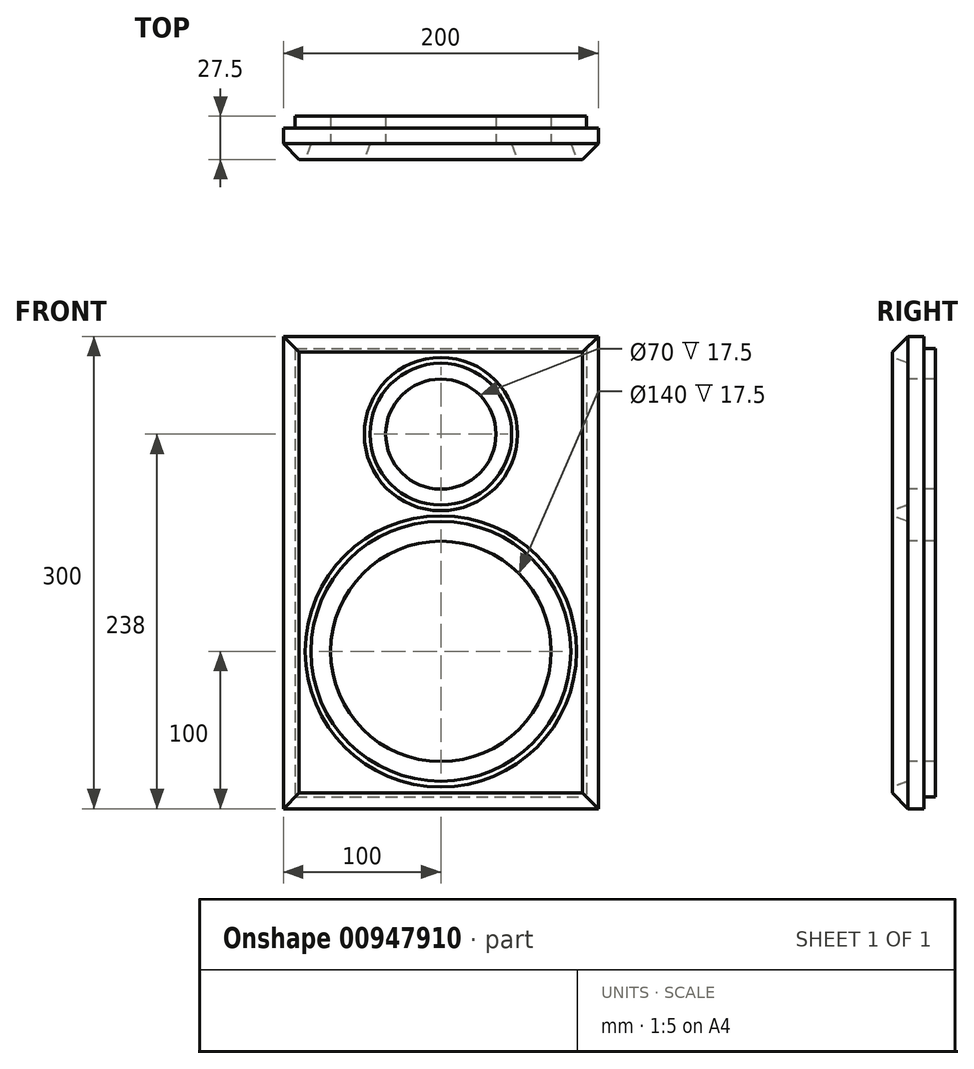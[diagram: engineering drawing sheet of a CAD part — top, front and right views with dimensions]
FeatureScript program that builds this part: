
annotation { "Feature Type Name" : "Feature", "Feature Type Description" : "" }
export const myFeature = defineFeature(function(context is Context, id is Id, definition is map)
    precondition{}
    {
        {
            var Q0;
            Q0=qCreatedBy(makeId("Right.planeOp"),FACE);
            cPlane(context, id + "F0", {"entities" : qUnion([Q0]), "cplaneType" : CPlaneType.OFFSET, "offset" : 100 * mm, "width" : 150 * mm, "height" : 150 * mm});
        }
        {
            var Q0;
            Q0=qCreatedBy(makeId("Right.planeOp"),FACE);
            cPlane(context, id + "F1", {"entities" : qUnion([Q0]), "cplaneType" : CPlaneType.OFFSET, "offset" : 100 * mm, "oppositeDirection" : true, "width" : 150 * mm, "height" : 150 * mm});
        }
        {
            var Q0;
            Q0=qCreatedBy(makeId("Right.planeOp"),FACE);
            cPlane(context, id + "F2", {"entities" : qUnion([Q0]), "cplaneType" : CPlaneType.OFFSET, "offset" : (100 - 7.5) * mm, "width" : 150 * mm, "height" : 150 * mm});
        }
        {
            var Q0;
            Q0=qCreatedBy(makeId("Right.planeOp"),FACE);
            cPlane(context, id + "F3", {"entities" : qUnion([Q0]), "cplaneType" : CPlaneType.OFFSET, "offset" : (100 - 7.5) * mm, "oppositeDirection" : true, "width" : 150 * mm, "height" : 150 * mm});
        }
        {
            var Q0;
            Q0=qCreatedBy(makeId("Top.planeOp"),FACE);
            cPlane(context, id + "F4", {"entities" : qUnion([Q0]), "cplaneType" : CPlaneType.OFFSET, "offset" : 7.7 * mm, "width" : 150 * mm, "height" : 150 * mm});
        }
        {
            var Q0;
            Q0=qCreatedBy(makeId("Top.planeOp"),FACE);
            cPlane(context, id + "F5", {"entities" : qUnion([Q0]), "cplaneType" : CPlaneType.OFFSET, "offset" : 300 * mm, "width" : 150 * mm, "height" : 150 * mm});
        }
        {
            var Q0;
            Q0=qCreatedBy(makeId("Top.planeOp"),FACE);
            cPlane(context, id + "F6", {"entities" : qUnion([Q0]), "cplaneType" : CPlaneType.OFFSET, "offset" : (300 - 7.5) * mm, "width" : 150 * mm, "height" : 150 * mm});
        }
        {
            var Q0;
            Q0=qCreatedBy(makeId("Front.planeOp"),FACE);
            cPlane(context, id + "F7", {"entities" : qUnion([Q0]), "cplaneType" : CPlaneType.OFFSET, "offset" : 150 * mm, "width" : 150 * mm, "height" : 150 * mm});
        }
        {
            var Q0;
            Q0=qCreatedBy(makeId("Front.planeOp"),FACE);
            cPlane(context, id + "F8", {"entities" : qUnion([Q0]), "cplaneType" : CPlaneType.OFFSET, "offset" : (150 - 7.5) * mm, "width" : 150 * mm, "height" : 150 * mm});
        }
        {
            var Q0;
            Q0=qCreatedBy(id+"F8.planeOp",FACE);
            var sketch = newSketch(context, id + "F9", { "sketchPlane" : qUnion([Q0])});
            skLineSegment(sketch, "E0.bottom", {"start": v(-92.5, 292.5) * mm, "end": v(92.5, 292.5) * mm});
            skLineSegment(sketch, "E0.top", {"start": v(-92.5, 7.7) * mm, "end": v(92.5, 7.7) * mm});
            skLineSegment(sketch, "E0.left", {"start": v(-92.5, 292.5) * mm, "end": v(-92.5, 7.7) * mm});
            skLineSegment(sketch, "E0.right", {"start": v(92.5, 292.5) * mm, "end": v(92.5, 7.7) * mm});
            skSolve(sketch);
        }
        {
            var Q0;
            Q0=makeQuery(id+"F9.imprint","IMPRINT",FACE,{"disambiguationData":[TD([[makeQuery(id+"F9.imprint","IMPRINT",EDGE,{"derivedFrom":sQuery(id+"F9.wireOp",EDGE,"E0.bottom")}),-1.0]])]});
            extrude(context, id + "F10", {"entities" : qUnion([Q0]), "depth" : 7.5 * mm, "offsetDistance" : 25 * mm});
        }
        {
            var Q0;
            Q0=qCreatedBy(id+"F7.planeOp",FACE);
            var sketch = newSketch(context, id + "F11", { "sketchPlane" : qUnion([Q0])});
            skLineSegment(sketch, "E1.bottom", {"start": v(-100, 300) * mm, "end": v(100, 300) * mm});
            skLineSegment(sketch, "E1.top", {"start": v(-100, 0) * mm, "end": v(100, 0) * mm});
            skLineSegment(sketch, "E1.left", {"start": v(-100, 300) * mm, "end": v(-100, 0) * mm});
            skLineSegment(sketch, "E1.right", {"start": v(100, 300) * mm, "end": v(100, 0) * mm});
            skSolve(sketch);
        }
        {
            var Q0;
            Q0=makeQuery(id+"F11.imprint","IMPRINT",FACE,{"disambiguationData":[TD([[makeQuery(id+"F11.imprint","IMPRINT",EDGE,{"derivedFrom":sQuery(id+"F11.wireOp",EDGE,"E1.bottom")}),-1.0]])]});
            extrude(context, id + "F12", {"entities" : qUnion([Q0]), "operationType" : NewBodyOperationType.ADD, "depth" : 20 * mm, "offsetDistance" : 25 * mm});
        }
        {
            var Q0;
            Q0=qCreatedBy(id+"F0.planeOp",FACE);
            var sketch = newSketch(context, id + "F13", { "sketchPlane" : qUnion([Q0])});
            skLineSegment(sketch, "E2", {"start": v(-220, 0) * mm, "end": v(-220, 300) * mm});
            skLineSegment(sketch, "E3", {"start": v(-220, 300) * mm, "end": v(-180, 300) * mm});
            skLineSegment(sketch, "E4", {"start": v(-180, 300) * mm, "end": v(-180, 0) * mm});
            skLineSegment(sketch, "E5", {"start": v(-180, 0) * mm, "end": v(-220, 0) * mm});
            skSolve(sketch);
        }
        {
            var Q0;
            Q0=qCreatedBy(makeId("Front.planeOp"),FACE);
            cPlane(context, id + "F14", {"entities" : qUnion([Q0]), "cplaneType" : CPlaneType.OFFSET, "offset" : 300 * mm, "width" : 150 * mm, "height" : 150 * mm});
        }
        {
            var Q0;
            Q0=qCreatedBy(makeId("Front.planeOp"),FACE);
            cPlane(context, id + "F15", {"entities" : qUnion([Q0]), "cplaneType" : CPlaneType.OFFSET, "offset" : 160 * mm, "width" : 150 * mm, "height" : 150 * mm});
        }
        {
            var Q0;
            Q0=qCreatedBy(id+"F14.planeOp",FACE);
            var sketch = newSketch(context, id + "F16", { "sketchPlane" : qUnion([Q0])});
            skCircle(sketch, "E6", {"center": v(0, 100) * mm, "radius": 70 * mm});
            skSolve(sketch);
        }
        {
            var Q0;
            Q0=qSketchRegion(id+"F16",true);
            var Q1;
            Q1=qCreatedBy(id+"F8.planeOp",FACE);
            extrude(context, id + "F17", {"entities" : qUnion([Q0]), "operationType" : NewBodyOperationType.REMOVE, "endBound" : BoundingType.UP_TO_SURFACE, "oppositeDirection" : true, "depth" : 25 * mm, "endBoundEntityFace" : qUnion([Q1]), "offsetDistance" : 25 * mm});
        }
        {
            var Q0;
            Q0=qCreatedBy(id+"F14.planeOp",FACE);
            var sketch = newSketch(context, id + "F18", { "sketchPlane" : qUnion([Q0])});
            skCircle(sketch, "E7", {"center": v(0, 100) * mm, "radius": 82.5 * mm});
            skSolve(sketch);
        }
        {
            var Q0;
            Q0=qSketchRegion(id+"F18",true);
            var Q1;
            Q1=qCreatedBy(id+"F15.planeOp",FACE);
            extrude(context, id + "F19", {"entities" : qUnion([Q0]), "operationType" : NewBodyOperationType.REMOVE, "endBound" : BoundingType.UP_TO_SURFACE, "oppositeDirection" : true, "depth" : 25 * mm, "endBoundEntityFace" : qUnion([Q1]), "offsetDistance" : 25 * mm});
        }
        {
            var Q0;
            Q0=qCreatedBy(id+"F14.planeOp",FACE);
            var sketch = newSketch(context, id + "F20", { "sketchPlane" : qUnion([Q0])});
            skCircle(sketch, "E8", {"center": v(0, 238) * mm, "radius": 35 * mm});
            skSolve(sketch);
        }
        {
            var Q0;
            Q0=makeQuery(id+"F20.imprint","IMPRINT",FACE,{"disambiguationData":[TD([[makeQuery(id+"F20.imprint","IMPRINT",EDGE,{"derivedFrom":sQuery(id+"F20.wireOp",EDGE,"E8")}),1.0]])]});
            var Q1;
            Q1=qCreatedBy(id+"F8.planeOp",FACE);
            extrude(context, id + "F21", {"entities" : qUnion([Q0]), "operationType" : NewBodyOperationType.REMOVE, "endBound" : BoundingType.UP_TO_SURFACE, "oppositeDirection" : true, "depth" : 25 * mm, "endBoundEntityFace" : qUnion([Q1]), "offsetDistance" : 25 * mm});
        }
        {
            var Q0;
            Q0=qCreatedBy(id+"F14.planeOp",FACE);
            var sketch = newSketch(context, id + "F22", { "sketchPlane" : qUnion([Q0])});
            skCircle(sketch, "E9", {"center": v(0, 238) * mm, "radius": 45 * mm});
            skSolve(sketch);
        }
        {
            var Q0;
            Q0=qSketchRegion(id+"F22",true);
            var Q1;
            Q1=qCreatedBy(id+"F15.planeOp",FACE);
            extrude(context, id + "F23", {"entities" : qUnion([Q0]), "operationType" : NewBodyOperationType.REMOVE, "endBound" : BoundingType.UP_TO_SURFACE, "oppositeDirection" : true, "depth" : 25 * mm, "endBoundEntityFace" : qUnion([Q1]), "offsetDistance" : 25 * mm});
        }
        {
            var Q0;
            Q0=makeQuery(id+"F13.imprint","IMPRINT",FACE,{"disambiguationData":[TD([[makeQuery(id+"F13.imprint","IMPRINT",EDGE,{"derivedFrom":sQuery(id+"F13.wireOp",EDGE,"E2")}),-1.0]])]});
            var Q1;
            Q1=qCreatedBy(id+"F1.planeOp",FACE);
            extrude(context, id + "F24", {"entities" : qUnion([Q0]), "operationType" : NewBodyOperationType.REMOVE, "endBound" : BoundingType.UP_TO_SURFACE, "oppositeDirection" : true, "depth" : 25 * mm, "endBoundEntityFace" : qUnion([Q1]), "offsetDistance" : 25 * mm});
        }
        {
            var Q0;
            Q0=makeQuery(id+"F12.opExtrude","CAP_EDGE",EDGE,{"disambiguationData":[OSD([sQuery(id+"F11.wireOp",EDGE,"E1.right")])],"isStart":false});
            var Q1;
            Q1=makeQuery(id+"F12.opExtrude","CAP_EDGE",EDGE,{"disambiguationData":[OSD([sQuery(id+"F11.wireOp",EDGE,"E1.bottom")])],"isStart":false});
            var Q2;
            Q2=makeQuery(id+"F12.opExtrude","CAP_EDGE",EDGE,{"disambiguationData":[OSD([sQuery(id+"F11.wireOp",EDGE,"E1.left")])],"isStart":false});
            var Q3;
            Q3=makeQuery(id+"F12.opExtrude","CAP_EDGE",EDGE,{"disambiguationData":[OSD([sQuery(id+"F11.wireOp",EDGE,"E1.top")])],"isStart":false});
            chamfer(context, id + "F25", {"entities" : qUnion([Q0, Q1, Q2, Q3]), "width" : 10 * mm, "tangentPropagation" : true});
        }
        {
            var Q0;
            Q0=makeQuery(id+"F19.boolean.opBoolean","INTERSECT",EDGE,{"derivedFrom":[makeQuery(id+"F12.opExtrude","CAP_FACE",FACE,{"disambiguationData":[OSD([sQuery(id+"F11.wireOp",EDGE,"E1.bottom"),sQuery(id+"F11.wireOp",EDGE,"E1.top"),sQuery(id+"F11.wireOp",EDGE,"E1.left"),sQuery(id+"F11.wireOp",EDGE,"E1.right")])],"isStart":false}),makeQuery(id+"F19.opExtrude","SWEPT_FACE",FACE,{"disambiguationData":[OSD([sQuery(id+"F18.wireOp",EDGE,"E7")])]})]});
            chamfer(context, id + "F26", {"entities" : qUnion([Q0]), "chamferType" : ChamferType.OFFSET_ANGLE, "width" : 10 * mm, "oppositeDirection" : false, "angle" : 20 * degree, "tangentPropagation" : true});
        }
        {
            var Q0;
            Q0=makeQuery(id+"F23.boolean.opBoolean","INTERSECT",EDGE,{"derivedFrom":[makeQuery(id+"F12.opExtrude","CAP_FACE",FACE,{"disambiguationData":[OSD([sQuery(id+"F11.wireOp",EDGE,"E1.bottom"),sQuery(id+"F11.wireOp",EDGE,"E1.top"),sQuery(id+"F11.wireOp",EDGE,"E1.left"),sQuery(id+"F11.wireOp",EDGE,"E1.right")])],"isStart":false}),makeQuery(id+"F23.opExtrude","SWEPT_FACE",FACE,{"disambiguationData":[OSD([sQuery(id+"F22.wireOp",EDGE,"E9")])]})]});
            chamfer(context, id + "F27", {"entities" : qUnion([Q0]), "chamferType" : ChamferType.OFFSET_ANGLE, "width" : 10 * mm, "oppositeDirection" : false, "angle" : 20 * degree, "tangentPropagation" : true});
        }
    });
